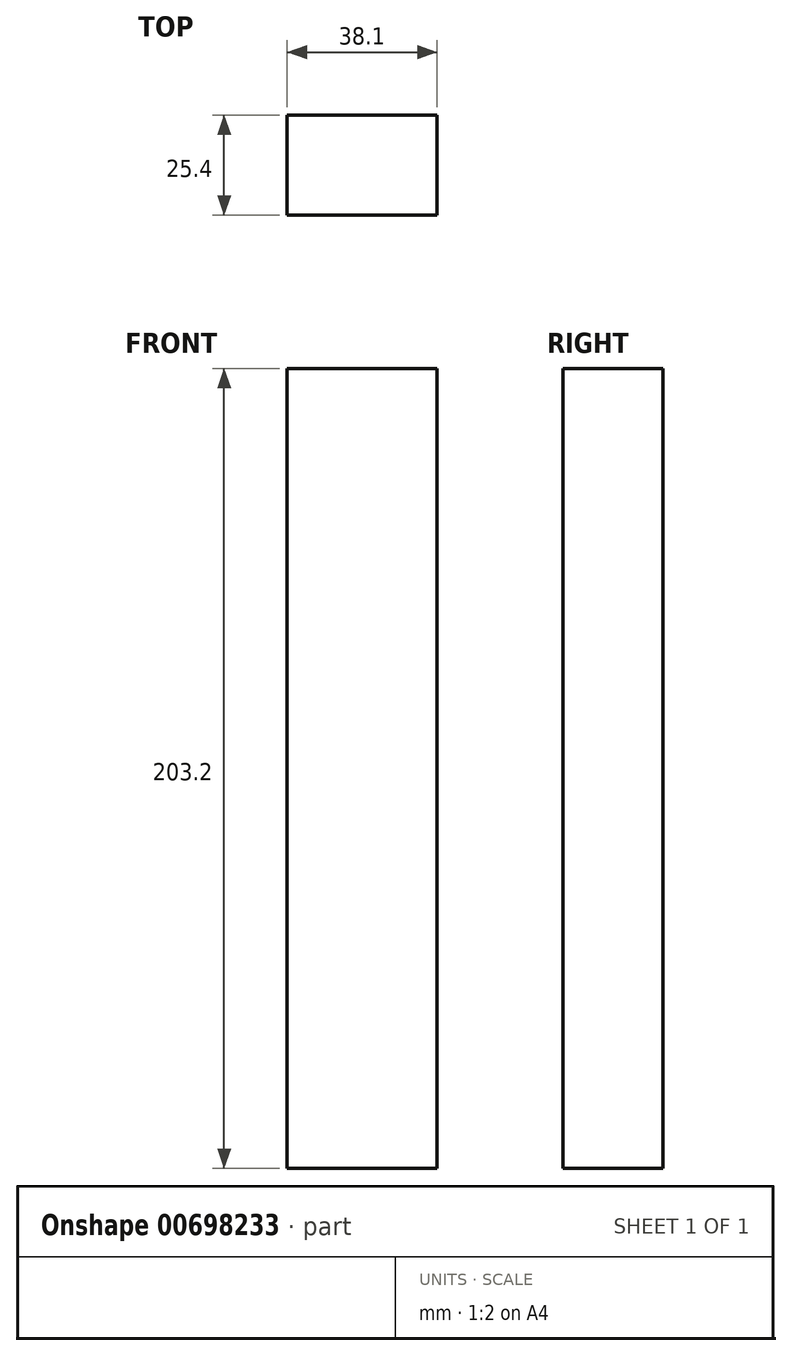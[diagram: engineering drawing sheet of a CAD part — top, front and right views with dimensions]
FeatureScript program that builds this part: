
annotation { "Feature Type Name" : "Feature", "Feature Type Description" : "" }
export const myFeature = defineFeature(function(context is Context, id is Id, definition is map)
    precondition{}
    {
        {
            var Q0;
            Q0=qCreatedBy(makeId("Front.planeOp"),FACE);
            var sketch = newSketch(context, id + "F0", { "sketchPlane" : qUnion([Q0])});
            skLineSegment(sketch, "E0.bottom", {"start": v(-120.72, 114.96) * mm, "end": v(-82.62, 114.96) * mm});
            skLineSegment(sketch, "E0.top", {"start": v(-120.72, -88.24) * mm, "end": v(-82.62, -88.24) * mm});
            skLineSegment(sketch, "E0.left", {"start": v(-120.72, 114.96) * mm, "end": v(-120.72, -88.24) * mm});
            skLineSegment(sketch, "E0.right", {"start": v(-82.62, 114.96) * mm, "end": v(-82.62, -88.24) * mm});
            skSolve(sketch);
        }
        {
            var Q0;
            Q0 = qSketchRegion(id + "F0", true);
            extrude(context, id + "F1", {"entities" : qUnion([Q0]), "depth" : 25.4 * mm, "offsetDistance" : 25.4 * mm});
        }
    });
